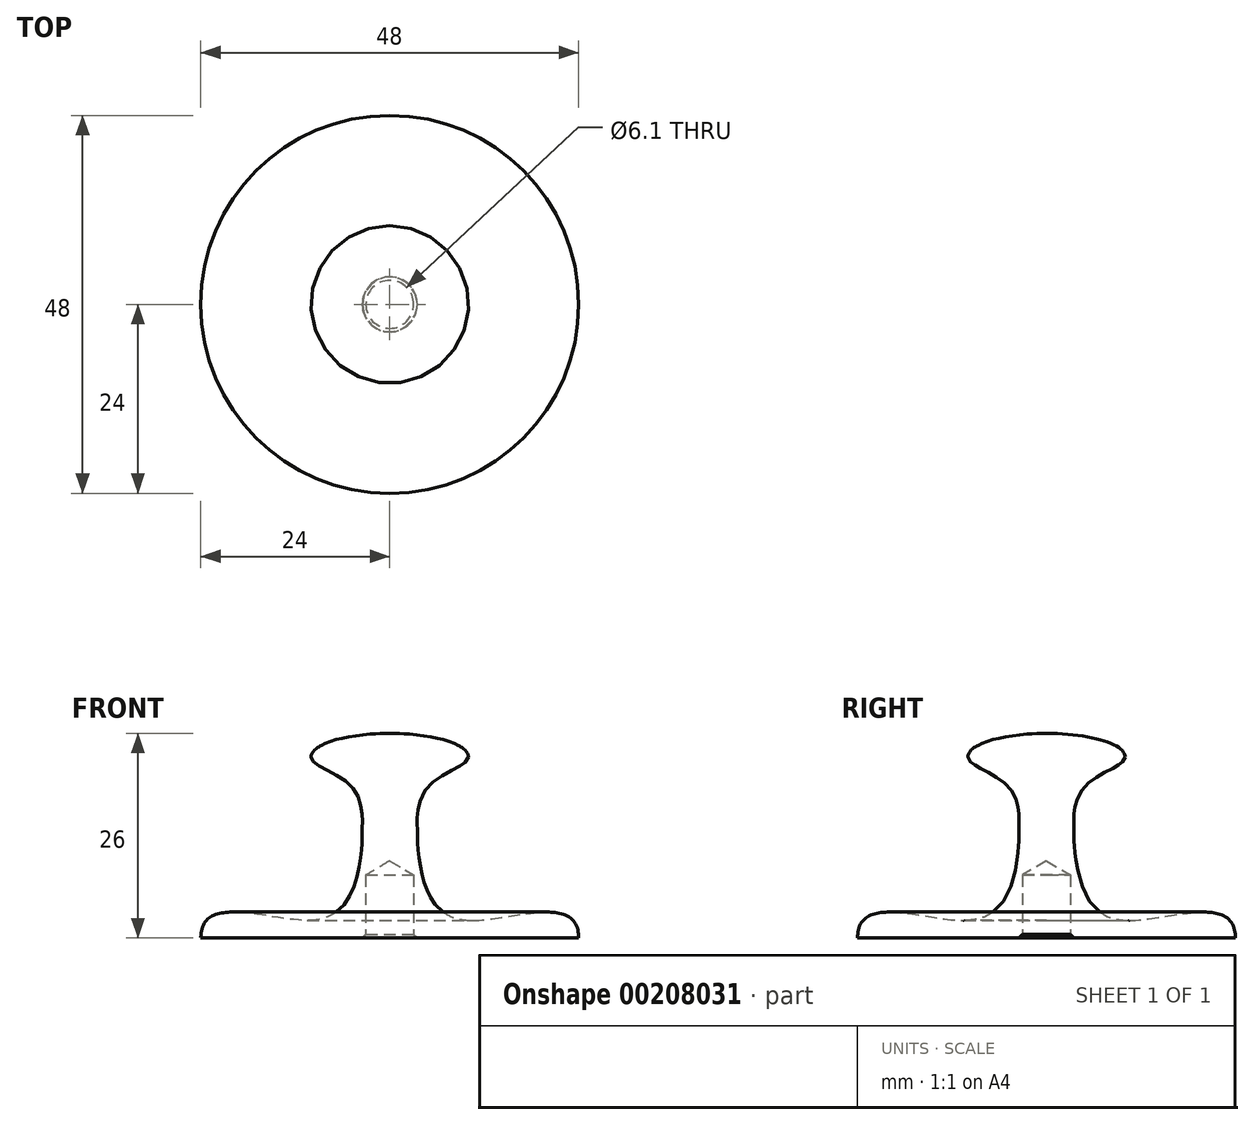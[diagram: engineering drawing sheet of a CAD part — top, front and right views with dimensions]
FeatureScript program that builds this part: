
annotation { "Feature Type Name" : "Feature", "Feature Type Description" : "" }
export const myFeature = defineFeature(function(context is Context, id is Id, definition is map)
    precondition{}
    {
        {
            var Q0;
            Q0=qCreatedBy(makeId("Right.planeOp"),FACE);
            var sketch = newSketch(context, id + "F0", { "sketchPlane" : qUnion([Q0])});
            skEllipticalArc(sketch, "E0", {});
            skLineSegment(sketch, "E1", {"start": v(0, 0) * mm, "end": v(0, 26) * mm});
            skLineSegment(sketch, "E2", {"start": v(0, 0) * mm, "end": v(24, 0) * mm});
            skFitSpline(sketch, "E3", {"points": [v(10, 23) * mm, v(4.77, 19.15) * mm, v(3.5, 13.83) * mm, v(3.5, 12.97) * mm, v(3.9, 9) * mm, v(9.35, 2.31) * mm, v(24, 0) * mm], "startDerivative": vector(0, -19.48) * mm, "endDerivative": vector(0, -70.27) * mm});
            skLineSegment(sketch, "E4", {"start": v(3.5, -2.75) * mm, "end": v(3.5, 30.42) * mm, "construction": true});
            skLineSegment(sketch, "E5", {"start": v(25.91, 3.3) * mm, "end": v(-12.6, 3.3) * mm, "construction": true});
            skLineSegment(sketch, "E6", {"start": v(24, 0) * mm, "end": v(24, 12.36) * mm, "construction": true});
            skLineSegment(sketch, "E7", {"start": v(10, 23) * mm, "end": v(10, 20.73) * mm, "construction": true});
            const initialGuessF0  = {"E0": [0, 0.023, -1, 0, 0.01, 0.003, 3.141592653589793, 4.71238898038469]};
            skSetInitialGuess(sketch, initialGuessF0);
            skSolve(sketch);
        }
        {
            var Q0;
            Q0 = qSketchRegion(id + "F0", true);
            var Q1;
            Q1=sQuery(id+"F0.wireOp",EDGE,"E1");
            revolve(context, id + "F1", {"entities" : qUnion([Q0]), "axis" : qUnion([Q1]), "revolveType" : RevolveType.FULL});
        }
        {
            var Q0;
            Q0=makeQuery(id+"F1.opRevolve","SWEPT_FACE",FACE,{"disambiguationData":[OSD([sQuery(id+"F0.wireOp",EDGE,"E2")])]});
            var sketch = newSketch(context, id + "F2", { "sketchPlane" : qUnion([Q0])});
            skPoint(sketch, "E8", {"position": v(0, 0) * mm});
            skSolve(sketch);
        }
        {
            var Q0;
            Q0=sQuery(id+"F2.wireOp",VERTEX,"E8");
            var Q1;
            Q1=makeQuery(id+"F1.opRevolve","SWEPT_BODY",BODY,{"disambiguationData":[OSD([sQuery(id+"F0.wireOp",EDGE,"E0"),sQuery(id+"F0.wireOp",EDGE,"E1"),sQuery(id+"F0.wireOp",EDGE,"E2"),sQuery(id+"F0.wireOp",EDGE,"E3")])]});
            hole(context, id + "F3", {"style" : HoleStyle.C_SINK, "endStyle" : HoleEndStyle.BLIND, "holeDiameter" : 6.1 * mm, "cSinkDiameter" : 7 * mm, "cSinkAngle" : 90 * degree, "holeDepth" : 8 * mm, "locations" : qUnion([Q0]), "scope" : qUnion([Q1]), "tappedDepth" : 12 * mm, "tapClearance" : 3});
        }
    });
